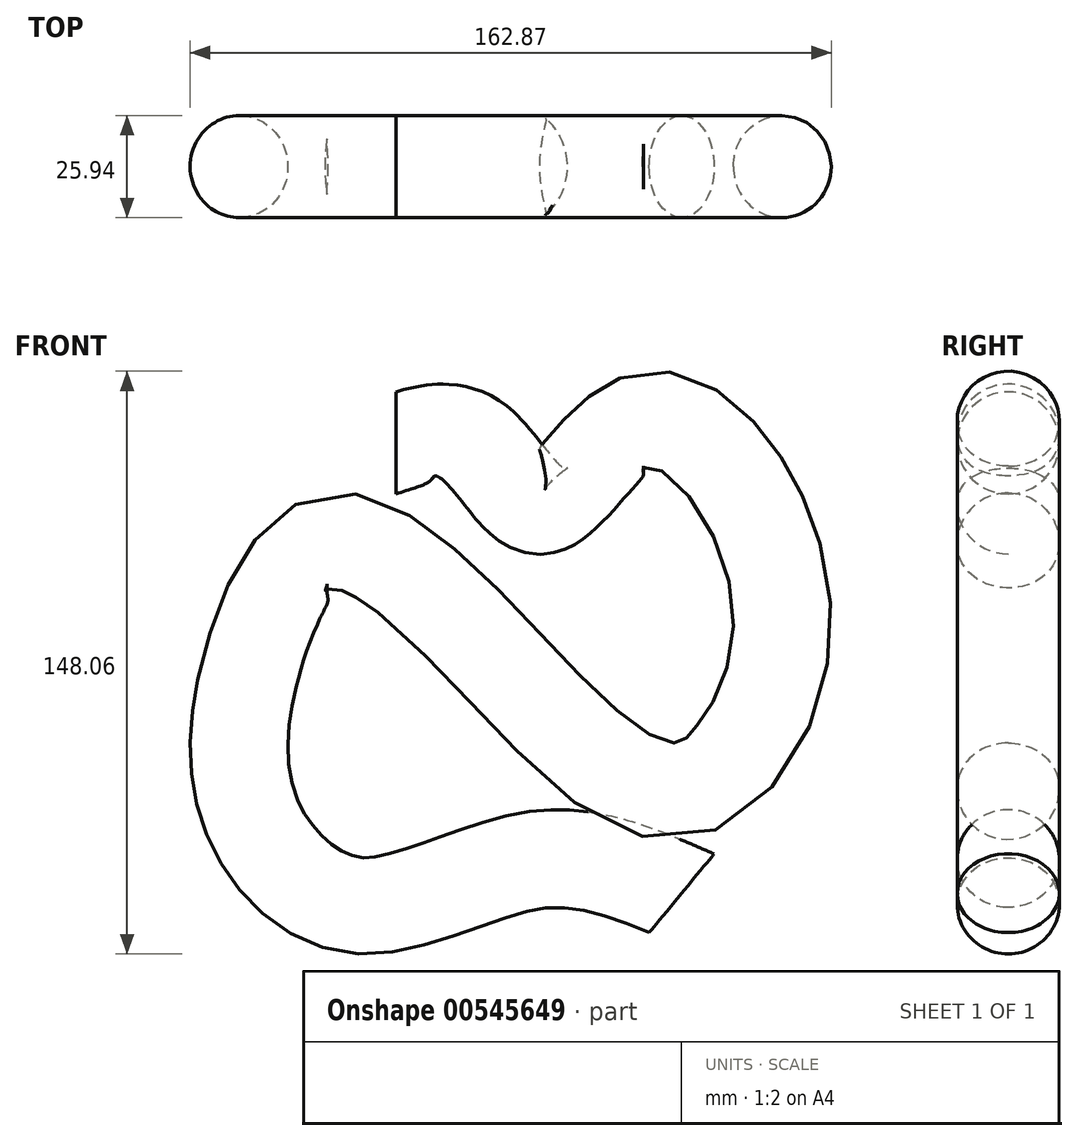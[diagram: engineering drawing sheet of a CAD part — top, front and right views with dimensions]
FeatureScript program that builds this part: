
annotation { "Feature Type Name" : "Feature", "Feature Type Description" : "" }
export const myFeature = defineFeature(function(context is Context, id is Id, definition is map)
    precondition{}
    {
        {
            var Q0;
            Q0=qCreatedBy(makeId("Right.planeOp"),FACE);
            var sketch = newSketch(context, id + "F0", { "sketchPlane" : qUnion([Q0])});
            skCircle(sketch, "E0", {"center": v(0, 49.09) * mm, "radius": 12.97 * mm});
            skSolve(sketch);
        }
        {
            var Q0;
            Q0=qCreatedBy(makeId("Front.planeOp"),FACE);
            var sketch = newSketch(context, id + "F1", { "sketchPlane" : qUnion([Q0])});
            skFitSpline(sketch, "E1", {"points": [v(0, 48.33) * mm, v(19.25, 48.37) * mm, v(37.05, 32.87) * mm, v(64.24, 53.7) * mm, v(97.15, 8.5) * mm, v(73.87, -37.66) * mm, v(34.57, -14.13) * mm, v(-15.55, 24.35) * mm, v(-37.4, -7.4) * mm, v(-36.51, -47.4) * mm, v(-9.7, -68.8) * mm, v(35.62, -57.75) * mm, v(72.14, -65.9) * mm], "startDerivative": vector(349.36, 103.42) * mm, "endDerivative": vector(433.6, -183.93) * mm});
            skSolve(sketch);
        }
        {
            var Q0;
            Q0 = qSketchRegion(id + "F0", true);
            var Q1;
            Q1 = qSketchRegion(id + "F1", true);
            var Q2;
            Q2 = qConstructionFilter(qBodyType(qCreatedBy(id + "F1" ,EDGE), BodyType.WIRE), ConstructionObject.NO);
            sweep(context, id + "F2", {"profiles" : qUnion([Q0, Q1]), "path" : qUnion([Q2])});
        }
    });
